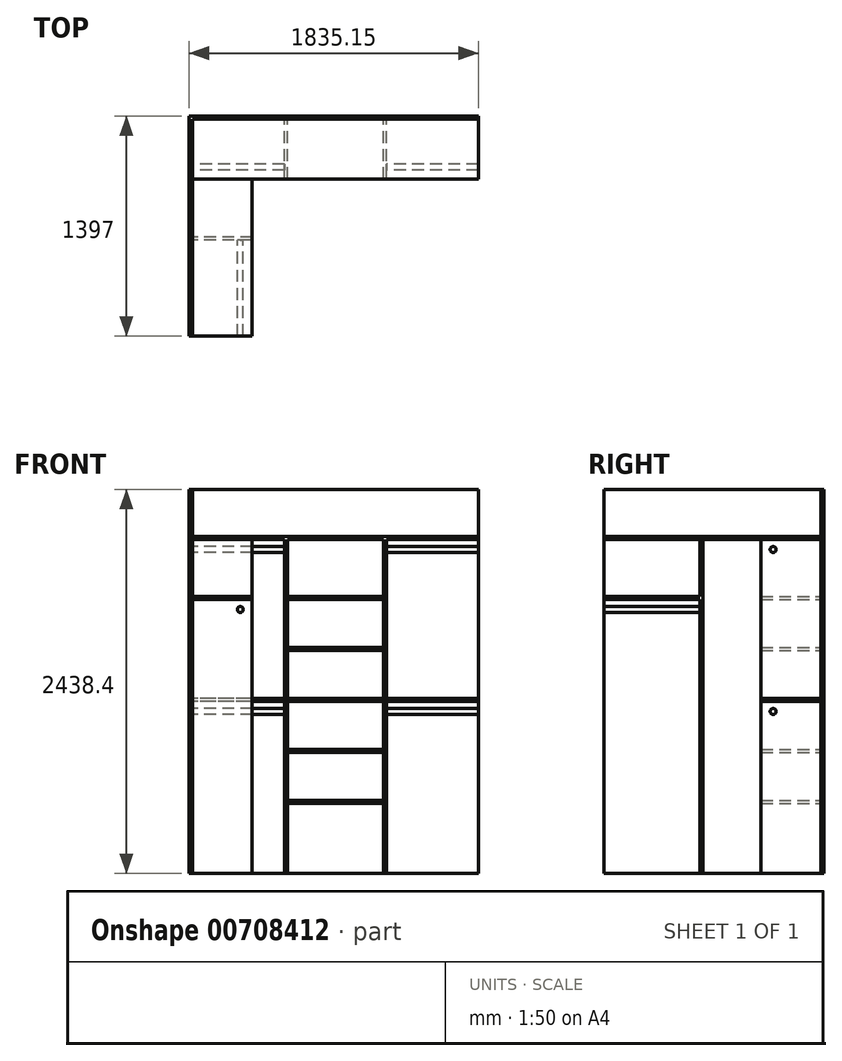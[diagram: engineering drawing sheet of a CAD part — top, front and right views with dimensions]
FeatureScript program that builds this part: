
annotation { "Feature Type Name" : "Feature", "Feature Type Description" : "" }
export const myFeature = defineFeature(function(context is Context, id is Id, definition is map)
    precondition{}
    {
        {
            var Q0;
            Q0=qCreatedBy(makeId("Front.planeOp"),FACE);
            var sketch = newSketch(context, id + "F0", { "sketchPlane" : qUnion([Q0])});
            skLineSegment(sketch, "E0.bottom", {"start": v(0, 0) * mm, "end": v(1816.1, 0) * mm});
            skLineSegment(sketch, "E0.top", {"start": v(0, 2438.4) * mm, "end": v(1816.1, 2438.4) * mm});
            skLineSegment(sketch, "E0.left", {"start": v(0, 0) * mm, "end": v(0, 2438.4) * mm});
            skLineSegment(sketch, "E0.right", {"start": v(1816.1, 0) * mm, "end": v(1816.1, 2438.4) * mm});
            skSolve(sketch);
        }
        {
            var Q0;
            Q0=makeQuery(id+"F0.imprint","IMPRINT",FACE,{"disambiguationData":[TD([[makeQuery(id+"F0.imprint","IMPRINT",EDGE,{"derivedFrom":sQuery(id+"F0.wireOp",EDGE,"E0.bottom")}),1.0]])]});
            extrude(context, id + "F1", {"entities" : qUnion([Q0]), "depth" : 19.05 * mm, "offsetDistance" : 25.4 * mm});
        }
        {
            var Q0;
            Q0=makeQuery(id+"F1.opExtrude","SWEPT_FACE",FACE,{"disambiguationData":[OSD([sQuery(id+"F0.wireOp",EDGE,"E0.left")])]});
            var sketch = newSketch(context, id + "F2", { "sketchPlane" : qUnion([Q0])});
            skLineSegment(sketch, "E1.bottom", {"start": v(0, 0) * mm, "end": v(1397, 0) * mm});
            skLineSegment(sketch, "E1.top", {"start": v(0, 2438.4) * mm, "end": v(1397, 2438.4) * mm});
            skLineSegment(sketch, "E1.left", {"start": v(0, 0) * mm, "end": v(0, 2438.4) * mm});
            skLineSegment(sketch, "E1.right", {"start": v(1397, 0) * mm, "end": v(1397, 2438.4) * mm});
            skSolve(sketch);
        }
        {
            var Q0;
            Q0 = qSketchRegion(id + "F2", true);
            extrude(context, id + "F3", {"entities" : qUnion([Q0]), "operationType" : NewBodyOperationType.ADD, "depth" : 19.05 * mm, "offsetDistance" : 25.4 * mm});
        }
        {
            var Q0;
            Q0=makeQuery(id+"F3.opExtrude","CAP_FACE",FACE,{"disambiguationData":[OSD([sQuery(id+"F2.wireOp",EDGE,"E1.bottom"),sQuery(id+"F2.wireOp",EDGE,"E1.top"),sQuery(id+"F2.wireOp",EDGE,"E1.left"),sQuery(id+"F2.wireOp",EDGE,"E1.right")])],"isStart":true});
            var sketch = newSketch(context, id + "F4", { "sketchPlane" : qUnion([Q0])});
            skLineSegment(sketch, "E2", {"start": v(-19.05, 0) * mm, "end": v(-323.85, 0) * mm, "construction": true});
            skLineSegment(sketch, "E3", {"start": v(-323.85, 0) * mm, "end": v(-323.85, 1028.7) * mm, "construction": true});
            skLineSegment(sketch, "E4", {"start": v(-323.85, 1028.7) * mm, "end": v(-323.85, 2057.4) * mm, "construction": true});
            skCircle(sketch, "E5", {"center": v(-323.85, 2057.4) * mm, "radius": 19.05 * mm});
            skLineSegment(sketch, "E6", {"start": v(-323.85, 2057.4) * mm, "end": v(-323.85, 2120.9) * mm, "construction": true});
            skCircle(sketch, "E7", {"center": v(-323.85, 1028.7) * mm, "radius": 19.05 * mm});
            skLineSegment(sketch, "E8.bottom", {"start": v(-400.05, 2139.95) * mm, "end": v(-19.05, 2139.95) * mm, "construction": true});
            skLineSegment(sketch, "E8.top", {"start": v(-400.05, 2120.9) * mm, "end": v(-19.05, 2120.9) * mm, "construction": true});
            skLineSegment(sketch, "E8.left", {"start": v(-400.05, 2139.95) * mm, "end": v(-400.05, 2120.9) * mm, "construction": true});
            skLineSegment(sketch, "E8.right", {"start": v(-19.05, 2139.95) * mm, "end": v(-19.05, 2120.9) * mm, "construction": true});
            skLineSegment(sketch, "E9.bottom", {"start": v(-400.05, 1111.25) * mm, "end": v(-19.05, 1111.25) * mm});
            skLineSegment(sketch, "E9.top", {"start": v(-400.05, 1092.2) * mm, "end": v(-19.05, 1092.2) * mm});
            skLineSegment(sketch, "E9.left", {"start": v(-400.05, 1111.25) * mm, "end": v(-400.05, 1092.2) * mm});
            skLineSegment(sketch, "E9.right", {"start": v(-19.05, 1111.25) * mm, "end": v(-19.05, 1092.2) * mm});
            skSolve(sketch);
        }
        {
            var Q0;
            Q0 = qSketchRegion(id + "F4", true);
            extrude(context, id + "F5", {"entities" : qUnion([Q0]), "depth" : 584.2 * mm, "offsetDistance" : 25.4 * mm});
        }
        {
            var Q0;
            Q0=makeQuery(id+"F1.opExtrude","CAP_FACE",FACE,{"disambiguationData":[OSD([sQuery(id+"F0.wireOp",EDGE,"E0.bottom"),sQuery(id+"F0.wireOp",EDGE,"E0.top"),sQuery(id+"F0.wireOp",EDGE,"E0.left"),sQuery(id+"F0.wireOp",EDGE,"E0.right")])],"isStart":false});
            var sketch = newSketch(context, id + "F6", { "sketchPlane" : qUnion([Q0])});
            skLineSegment(sketch, "E10.bottom", {"start": v(584.2, 0) * mm, "end": v(603.25, 0) * mm});
            skLineSegment(sketch, "E10.top", {"start": v(584.2, 2120.9) * mm, "end": v(603.25, 2120.9) * mm});
            skLineSegment(sketch, "E10.left", {"start": v(584.2, 0) * mm, "end": v(584.2, 2120.9) * mm});
            skLineSegment(sketch, "E10.right", {"start": v(603.25, 0) * mm, "end": v(603.25, 2120.9) * mm});
            skLineSegment(sketch, "E11.bottom", {"start": v(1231.9, 0) * mm, "end": v(1212.85, 0) * mm});
            skLineSegment(sketch, "E11.top", {"start": v(1231.9, 2120.9) * mm, "end": v(1212.85, 2120.9) * mm});
            skLineSegment(sketch, "E11.left", {"start": v(1231.9, 0) * mm, "end": v(1231.9, 2120.9) * mm});
            skLineSegment(sketch, "E11.right", {"start": v(1212.85, 0) * mm, "end": v(1212.85, 2120.9) * mm});
            skLineSegment(sketch, "E12.bottom", {"start": v(1816.1, 2139.95) * mm, "end": v(0, 2139.95) * mm});
            skLineSegment(sketch, "E12.top", {"start": v(1816.1, 2120.9) * mm, "end": v(0, 2120.9) * mm});
            skLineSegment(sketch, "E12.left", {"start": v(1816.1, 2139.95) * mm, "end": v(1816.1, 2120.9) * mm});
            skLineSegment(sketch, "E12.right", {"start": v(0, 2139.95) * mm, "end": v(0, 2120.9) * mm});
            skSolve(sketch);
        }
        {
            var Q0;
            Q0 = qSketchRegion(id + "F6", true);
            extrude(context, id + "F7", {"entities" : qUnion([Q0]), "depth" : 381 * mm, "offsetDistance" : 25.4 * mm});
        }
        {
            var Q0;
            Q0=makeQuery(id+"F1.opExtrude","CAP_FACE",FACE,{"disambiguationData":[OSD([sQuery(id+"F0.wireOp",EDGE,"E0.bottom"),sQuery(id+"F0.wireOp",EDGE,"E0.top"),sQuery(id+"F0.wireOp",EDGE,"E0.left"),sQuery(id+"F0.wireOp",EDGE,"E0.right")])],"isStart":false});
            var sketch = newSketch(context, id + "F8", { "sketchPlane" : qUnion([Q0])});
            skLineSegment(sketch, "E13.bottom", {"start": v(603.25, 1111.25) * mm, "end": v(1212.85, 1111.25) * mm});
            skLineSegment(sketch, "E13.top", {"start": v(603.25, 1092.2) * mm, "end": v(1212.85, 1092.2) * mm});
            skLineSegment(sketch, "E13.left", {"start": v(603.25, 1111.25) * mm, "end": v(603.25, 1092.2) * mm});
            skLineSegment(sketch, "E13.right", {"start": v(1212.85, 1111.25) * mm, "end": v(1212.85, 1092.2) * mm});
            skLineSegment(sketch, "E14.bottom", {"start": v(603.25, 787.4) * mm, "end": v(1212.85, 787.4) * mm});
            skLineSegment(sketch, "E14.top", {"start": v(603.25, 768.35) * mm, "end": v(1212.85, 768.35) * mm});
            skLineSegment(sketch, "E14.left", {"start": v(603.25, 787.4) * mm, "end": v(603.25, 768.35) * mm});
            skLineSegment(sketch, "E14.right", {"start": v(1212.85, 787.4) * mm, "end": v(1212.85, 768.35) * mm});
            skLineSegment(sketch, "E15", {"start": v(603.25, 768.35) * mm, "end": v(603.25, 0) * mm, "construction": true});
            skLineSegment(sketch, "E16", {"start": v(603.25, 0) * mm, "end": v(1212.85, 0) * mm, "construction": true});
            skLineSegment(sketch, "E17", {"start": v(1212.85, 0) * mm, "end": v(1212.85, 2117.32) * mm, "construction": true});
            skLineSegment(sketch, "E18", {"start": v(1212.85, 2117.32) * mm, "end": v(603.25, 2117.32) * mm, "construction": true});
            skLineSegment(sketch, "E19", {"start": v(603.25, 2117.32) * mm, "end": v(603.25, 686.88) * mm, "construction": true});
            skLineSegment(sketch, "E20.bottom", {"start": v(603.25, 1435.1) * mm, "end": v(1212.85, 1435.1) * mm});
            skLineSegment(sketch, "E20.top", {"start": v(603.25, 1416.05) * mm, "end": v(1212.85, 1416.05) * mm});
            skLineSegment(sketch, "E20.left", {"start": v(603.25, 1435.1) * mm, "end": v(603.25, 1416.05) * mm});
            skLineSegment(sketch, "E20.right", {"start": v(1212.85, 1435.1) * mm, "end": v(1212.85, 1416.05) * mm});
            skLineSegment(sketch, "E21.bottom", {"start": v(603.25, 1758.95) * mm, "end": v(1212.85, 1758.95) * mm});
            skLineSegment(sketch, "E21.top", {"start": v(603.25, 1739.9) * mm, "end": v(1212.85, 1739.9) * mm});
            skLineSegment(sketch, "E21.left", {"start": v(603.25, 1758.95) * mm, "end": v(603.25, 1739.9) * mm});
            skLineSegment(sketch, "E21.right", {"start": v(1212.85, 1758.95) * mm, "end": v(1212.85, 1739.9) * mm});
            skLineSegment(sketch, "E22.bottom", {"start": v(603.25, 463.55) * mm, "end": v(1212.85, 463.55) * mm});
            skLineSegment(sketch, "E22.top", {"start": v(603.25, 444.5) * mm, "end": v(1212.85, 444.5) * mm});
            skLineSegment(sketch, "E22.left", {"start": v(603.25, 463.55) * mm, "end": v(603.25, 444.5) * mm});
            skLineSegment(sketch, "E22.right", {"start": v(1212.85, 463.55) * mm, "end": v(1212.85, 444.5) * mm});
            skLineSegment(sketch, "E23.bottom", {"start": v(1816.1, 1111.25) * mm, "end": v(1231.9, 1111.25) * mm});
            skLineSegment(sketch, "E23.top", {"start": v(1816.1, 1092.2) * mm, "end": v(1231.9, 1092.2) * mm});
            skLineSegment(sketch, "E23.left", {"start": v(1816.1, 1111.25) * mm, "end": v(1816.1, 1092.2) * mm});
            skLineSegment(sketch, "E23.right", {"start": v(1231.9, 1111.25) * mm, "end": v(1231.9, 1092.2) * mm});
            skSolve(sketch);
        }
        {
            var Q0;
            Q0 = qSketchRegion(id + "F8", true);
            extrude(context, id + "F9", {"entities" : qUnion([Q0]), "depth" : 381 * mm, "offsetDistance" : 25.4 * mm});
        }
        {
            var Q0;
            Q0=makeQuery(id+"F7.opExtrude","CAP_FACE",FACE,{"disambiguationData":[OSD([sQuery(id+"F6.wireOp",EDGE,"E10.bottom"),sQuery(id+"F6.wireOp",EDGE,"E10.left"),sQuery(id+"F6.wireOp",EDGE,"E10.right"),sQuery(id+"F6.wireOp",EDGE,"E11.bottom"),sQuery(id+"F6.wireOp",EDGE,"E11.left"),sQuery(id+"F6.wireOp",EDGE,"E11.right"),sQuery(id+"F6.wireOp",EDGE,"E12.bottom"),sQuery(id+"F6.wireOp",EDGE,"E12.top"),sQuery(id+"F6.wireOp",EDGE,"E12.left"),sQuery(id+"F6.wireOp",EDGE,"E12.right")])],"isStart":false});
            var sketch = newSketch(context, id + "F10", { "sketchPlane" : qUnion([Q0])});
            skLineSegment(sketch, "E24.bottom", {"start": v(0, 2139.95) * mm, "end": v(381, 2139.95) * mm});
            skLineSegment(sketch, "E24.top", {"start": v(0, 2120.9) * mm, "end": v(381, 2120.9) * mm});
            skLineSegment(sketch, "E24.left", {"start": v(0, 2139.95) * mm, "end": v(0, 2120.9) * mm});
            skLineSegment(sketch, "E24.right", {"start": v(381, 2139.95) * mm, "end": v(381, 2120.9) * mm});
            skSolve(sketch);
        }
        {
            var Q0;
            Q0 = qSketchRegion(id + "F10", true);
            var Q1;
            Q1=makeQuery(id+"F3.opExtrude","SWEPT_FACE",FACE,{"disambiguationData":[OSD([sQuery(id+"F2.wireOp",EDGE,"E1.right")])]});
            extrude(context, id + "F11", {"entities" : qUnion([Q0]), "endBound" : BoundingType.UP_TO_SURFACE, "depth" : 25.4 * mm, "endBoundEntityFace" : qUnion([Q1]), "offsetDistance" : 25.4 * mm});
        }
        {
            var Q0;
            Q0=makeQuery(id+"F3.opExtrude","CAP_FACE",FACE,{"disambiguationData":[OSD([sQuery(id+"F2.wireOp",EDGE,"E1.bottom"),sQuery(id+"F2.wireOp",EDGE,"E1.top"),sQuery(id+"F2.wireOp",EDGE,"E1.left"),sQuery(id+"F2.wireOp",EDGE,"E1.right")])],"isStart":true});
            var sketch = newSketch(context, id + "F12", { "sketchPlane" : qUnion([Q0])});
            skLineSegment(sketch, "E25.bottom", {"start": v(-787.4, 0) * mm, "end": v(-768.35, 0) * mm});
            skLineSegment(sketch, "E25.top", {"start": v(-787.4, 2120.9) * mm, "end": v(-768.35, 2120.9) * mm});
            skLineSegment(sketch, "E25.left", {"start": v(-787.4, 0) * mm, "end": v(-787.4, 2120.9) * mm});
            skLineSegment(sketch, "E25.right", {"start": v(-768.35, 0) * mm, "end": v(-768.35, 2120.9) * mm});
            skLineSegment(sketch, "E26", {"start": v(-1397, 0) * mm, "end": v(-1397, 1676.4) * mm, "construction": true});
            skLineSegment(sketch, "E27.bottom", {"start": v(-1397, 1758.95) * mm, "end": v(-787.4, 1758.95) * mm});
            skLineSegment(sketch, "E27.top", {"start": v(-1397, 1739.9) * mm, "end": v(-787.4, 1739.9) * mm});
            skLineSegment(sketch, "E27.left", {"start": v(-1397, 1758.95) * mm, "end": v(-1397, 1739.9) * mm});
            skLineSegment(sketch, "E27.right", {"start": v(-787.4, 1758.95) * mm, "end": v(-787.4, 1739.9) * mm});
            skSolve(sketch);
        }
        {
            var Q0;
            Q0 = qSketchRegion(id + "F12", true);
            extrude(context, id + "F13", {"entities" : qUnion([Q0]), "depth" : 381 * mm, "offsetDistance" : 25.4 * mm});
        }
        {
            var Q0;
            {var subQ0=sQuery(id+"F12.wireOp",EDGE,"E25.left");Q0=makeQuery(id+"F13.opExtrude","SWEPT_FACE",FACE,{"disambiguationData":[OSD([subQ0]),TDD([makeQuery(id+"F12.imprint","IMPRINT",EDGE,{"disambiguationData":[TD([[makeQuery(id+"F12.imprint","INTERSECT",VERTEX,{"derivedFrom":[makeQuery(id+"F3.opExtrude","CAP_EDGE",EDGE,{"disambiguationData":[OSD([sQuery(id+"F2.wireOp",EDGE,"E1.bottom")])],"isStart":true}),sQuery(id+"F12.wireOp",EDGE,"E25.bottom"),subQ0]}),-1.0]])],"derivedFrom":subQ0})])]});}
            var sketch = newSketch(context, id + "F14", { "sketchPlane" : qUnion([Q0])});
            skCircle(sketch, "E28", {"center": v(304.8, 1676.4) * mm, "radius": 19.05 * mm});
            skSolve(sketch);
        }
        {
            var Q0;
            Q0 = qSketchRegion(id + "F14", true);
            var Q1;
            Q1=makeQuery(id+"F3.opExtrude","SWEPT_FACE",FACE,{"disambiguationData":[OSD([sQuery(id+"F2.wireOp",EDGE,"E1.right")])]});
            extrude(context, id + "F15", {"entities" : qUnion([Q0]), "operationType" : NewBodyOperationType.ADD, "endBound" : BoundingType.UP_TO_SURFACE, "depth" : 25.4 * mm, "endBoundEntityFace" : qUnion([Q1]), "offsetDistance" : 25.4 * mm});
        }
        {
            var Q0;
            Q0=makeQuery(id+"F7.opExtrude","SWEPT_FACE",FACE,{"disambiguationData":[OSD([sQuery(id+"F6.wireOp",EDGE,"E11.left")])]});
            var sketch = newSketch(context, id + "F16", { "sketchPlane" : qUnion([Q0])});
            skCircle(sketch, "E29", {"center": v(-323.85, 2057.4) * mm, "radius": 19.05 * mm});
            skCircle(sketch, "E30", {"center": v(-323.85, 1028.7) * mm, "radius": 19.05 * mm});
            skSolve(sketch);
        }
        {
            var Q0;
            Q0 = qSketchRegion(id + "F16", true);
            var Q1;
            Q1=makeQuery(id+"F1.opExtrude","SWEPT_FACE",FACE,{"disambiguationData":[OSD([sQuery(id+"F0.wireOp",EDGE,"E0.right")])]});
            extrude(context, id + "F17", {"entities" : qUnion([Q0]), "operationType" : NewBodyOperationType.ADD, "endBound" : BoundingType.UP_TO_SURFACE, "depth" : 25.4 * mm, "endBoundEntityFace" : qUnion([Q1]), "offsetDistance" : 25.4 * mm});
        }
    });
